# Revit family: revolving-rd4a-1-secure-360
name_source: partatom
category: Doors
units: mm (PartAtom-declared; Revit-internal decimal feet)

## family parameters
Always vertical = Yes
Cut with Voids When Loaded = No
Host = Wall
OmniClass Number = 23.30.10.00
OmniClass Title = Doors
Room Calculation Point = No
Shared = No

## types (3) — shared parameters
Analytic Construction = <None>
BIMobject category = Revolving Doors
Brass Polished Finish = Brass, Polished
Brass Satin Finish = Brass, Satin
Ceiling Material = White Laminated
Clear Anodized = Clear Anodized
Dark Bronze Anodized = Dark Bronze Anodized
Date of publishing = 2015-02-23
Depth = 0.00
Disclaimer = Consult product specification for sensors to comply with ANSI A156.27.
Edition number = 1
Frame Material = Clear Anodized
Function = Interior
Glass = Glass
Height = 94 1/2"
IFC Classification = Door
Manufacturer name = Besam-North America
Material main = Aluminium
NBS Reference Code = 25-30-20-70
NBS Reference Description = Revolving Doorset Systems
Nominal height = 0.00
Nominal width = 0.00
Product SKU = RD4A
Product data url = http://besam-na.bimobject.com
Product family = Revolving
Product group = RD4A Series
QR code = http://besam-na.bimobject.com
Roof Material = Clear Anodized
Rough Height = 94 3/4"
Rubber = Rubber, Black
Stainless Steel Polished Finish = Stainless Steel, Polished
Stainless Steel Satin Finish = Stainless Steel, Satin
UNSPSC Code = 30171509
Uniclass 1.4 Code = L41112
Uniclass 1.4 Description = Revolving
Uniclass 2.0 Code = SS-25-30-20-70
Uniclass 2.0 Description = Revolving Doorset Systems
Wall Closure = By host
Weight Net (Kg) = 0

## per-type parameters (varying)
| type | Outer Radius | Rough Width | Width |
| RD4A-1-6 | 37 1/8" | 75 1/4" | 74 3/4" |
| RD4A-1-7 | 43 1/16" | 87 1/8" | 86 5/8" |
| RD4A-1-8 | 49" | 99" | 98 1/2" |

## geometry (parser evidence)
native form markers: Blend x4, Sweep x23
no freeform markers — native parametric forms only
